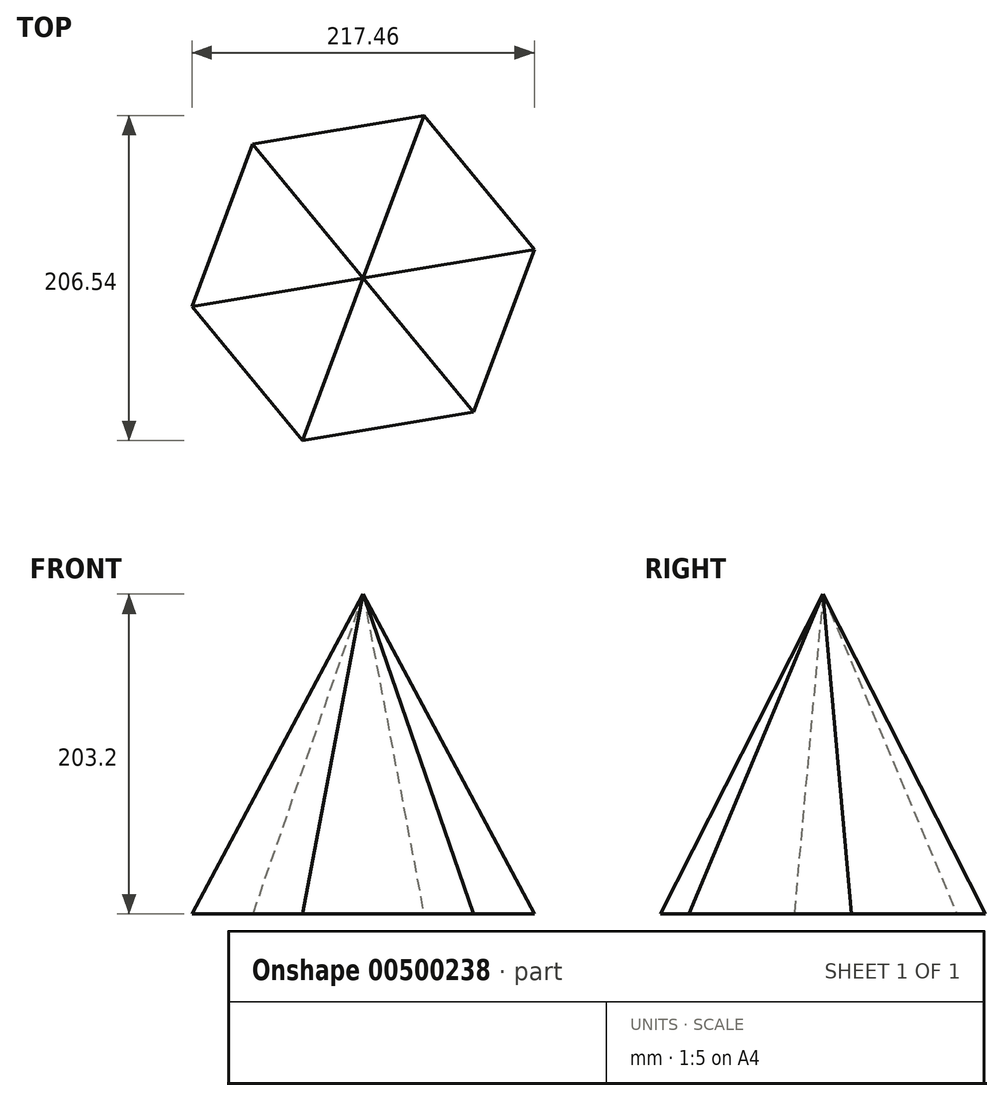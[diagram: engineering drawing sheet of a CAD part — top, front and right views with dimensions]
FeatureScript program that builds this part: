
annotation { "Feature Type Name" : "Feature", "Feature Type Description" : "" }
export const myFeature = defineFeature(function(context is Context, id is Id, definition is map)
    precondition{}
    {
        {
            var Q0;
            Q0=qCreatedBy(makeId("Top.planeOp"),FACE);
            var sketch = newSketch(context, id + "F0", { "sketchPlane" : qUnion([Q0])});
            skCircle(sketch, "E0.cCircle", {"center": v(0, 0) * mm, "radius": 110.25 * mm, "construction": true});
            skLineSegment(sketch, "E0.0", {"start": v(-108.73, -18.22) * mm, "end": v(-70.14, 85.05) * mm});
            skLineSegment(sketch, "E0.1", {"start": v(-70.14, 85.05) * mm, "end": v(38.59, 103.27) * mm});
            skLineSegment(sketch, "E0.2", {"start": v(38.59, 103.27) * mm, "end": v(108.73, 18.22) * mm});
            skLineSegment(sketch, "E0.3", {"start": v(108.73, 18.22) * mm, "end": v(70.14, -85.05) * mm});
            skLineSegment(sketch, "E0.4", {"start": v(70.14, -85.05) * mm, "end": v(-38.59, -103.27) * mm});
            skLineSegment(sketch, "E0.5", {"start": v(-38.59, -103.27) * mm, "end": v(-108.73, -18.22) * mm});
            skSolve(sketch);
        }
        {
            var Q0;
            Q0=qCreatedBy(makeId("Top.planeOp"),FACE);
            cPlane(context, id + "F1", {"entities" : qUnion([Q0]), "cplaneType" : CPlaneType.OFFSET, "offset" : 203.2 * mm, "width" : 150 * mm, "height" : 150 * mm});
        }
        {
            var Q0;
            Q0=qCreatedBy(id+"F1.planeOp",FACE);
            var sketch = newSketch(context, id + "F2", { "sketchPlane" : qUnion([Q0])});
            skPoint(sketch, "E1", {"position": v(0, 0) * mm});
            skSolve(sketch);
        }
        {
            var Q0;
            Q0=sQuery(id+"F2.wireOp",VERTEX,"E1");
            var Q1;
            Q1=makeQuery(id+"F0.imprint","IMPRINT",FACE,{"disambiguationData":[TD([[makeQuery(id+"F0.imprint","IMPRINT",EDGE,{"derivedFrom":sQuery(id+"F0.wireOp",EDGE,"E0.0")}),-1.0]])]});
            loft(context, id + "F3", {"sheetProfilesArray" : [{ "sheetProfileEntities" : qUnion([Q0]) }, { "sheetProfileEntities" : qUnion([Q1]) }]});
        }
    });
